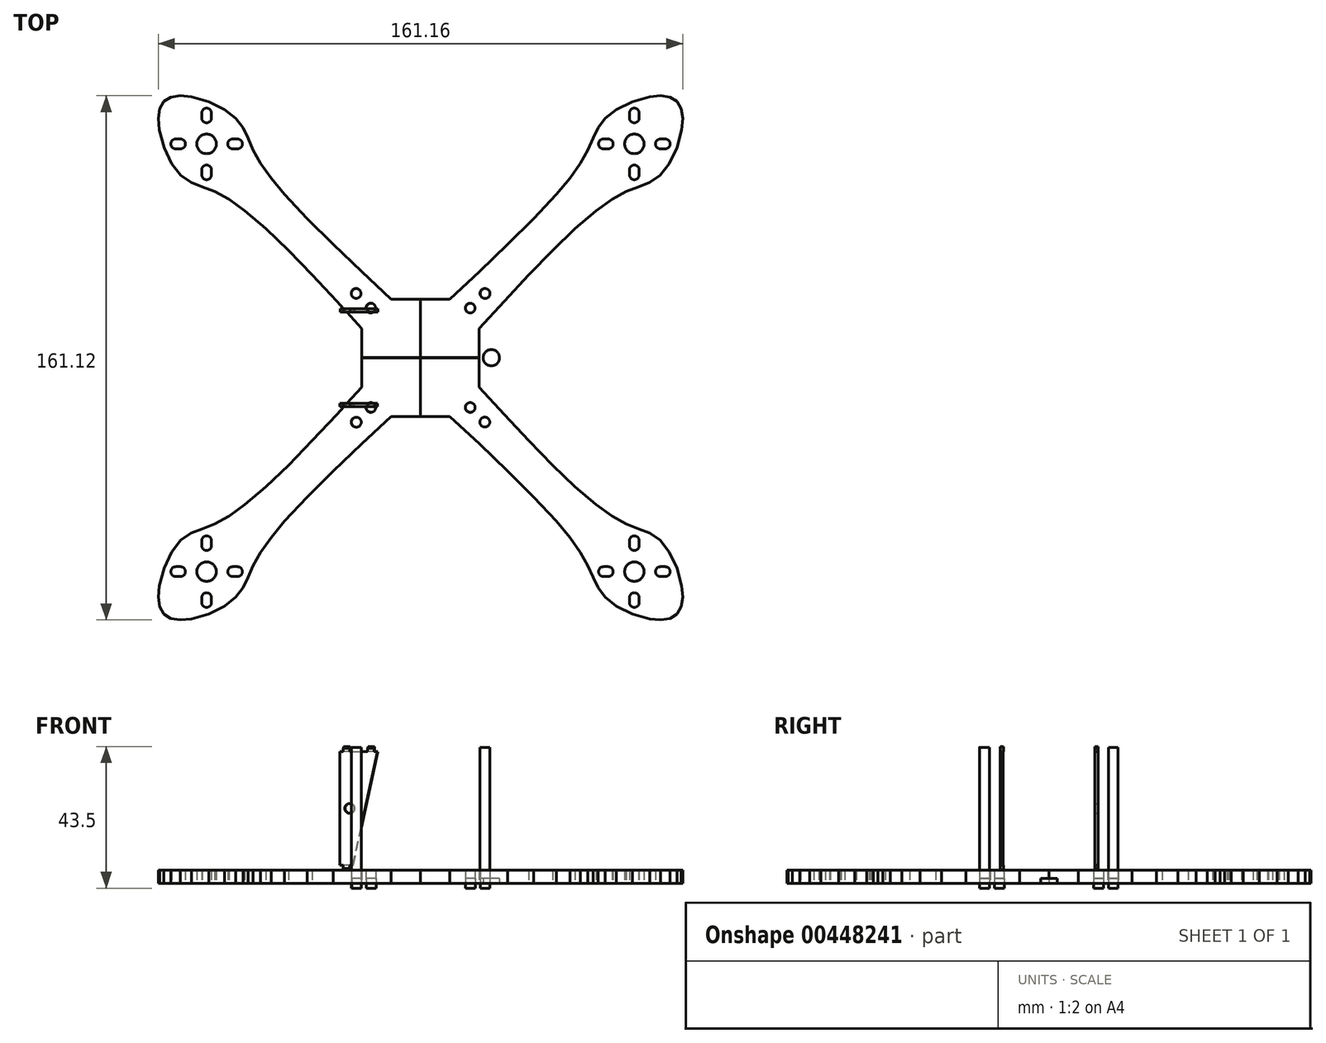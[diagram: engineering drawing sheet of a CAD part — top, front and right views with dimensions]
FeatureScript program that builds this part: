
annotation { "Feature Type Name" : "Feature", "Feature Type Description" : "" }
export const myFeature = defineFeature(function(context is Context, id is Id, definition is map)
    precondition{}
    {
        {
            var Q0;
            Q0=qCreatedBy(makeId("Top.planeOp"),FACE);
            var sketch = newSketch(context, id + "F0", { "sketchPlane" : qUnion([Q0])});
            skLineSegment(sketch, "E0", {"start": v(22.28, -31.26) * mm, "end": v(14.59, -22.9) * mm});
            skLineSegment(sketch, "E1", {"start": v(14.59, -22.9) * mm, "end": v(7.02, -14.81) * mm});
            skLineSegment(sketch, "E2", {"start": v(7.02, -14.81) * mm, "end": v(-0.3, -7.3) * mm});
            skLineSegment(sketch, "E3", {"start": v(-0.3, -7.3) * mm, "end": v(-7.23, -0.64) * mm});
            skLineSegment(sketch, "E4", {"start": v(-7.23, -0.64) * mm, "end": v(-13.66, 4.88) * mm});
            skLineSegment(sketch, "E5", {"start": v(-13.66, 4.88) * mm, "end": v(-18.55, 8.4) * mm});
            skLineSegment(sketch, "E6", {"start": v(-18.55, 8.4) * mm, "end": v(-22.93, 10.78) * mm});
            skLineSegment(sketch, "E7", {"start": v(-22.93, 10.78) * mm, "end": v(-26.8, 12.26) * mm});
            skLineSegment(sketch, "E8", {"start": v(-26.8, 12.26) * mm, "end": v(-30.23, 13.65) * mm});
            skLineSegment(sketch, "E9", {"start": v(-30.23, 13.65) * mm, "end": v(-33.32, 15.76) * mm});
            skLineSegment(sketch, "E10", {"start": v(-33.32, 15.76) * mm, "end": v(-36.16, 19.37) * mm});
            skLineSegment(sketch, "E11", {"start": v(-36.16, 19.37) * mm, "end": v(-38.52, 24.35) * mm});
            skLineSegment(sketch, "E12", {"start": v(-38.52, 24.35) * mm, "end": v(-40, 29.8) * mm});
            skLineSegment(sketch, "E13", {"start": v(-40, 29.8) * mm, "end": v(-40.28, 33.26) * mm});
            skLineSegment(sketch, "E14", {"start": v(-40.28, 33.26) * mm, "end": v(-39.85, 36.25) * mm});
            skLineSegment(sketch, "E15", {"start": v(-39.85, 36.25) * mm, "end": v(-38.57, 38.5) * mm});
            skLineSegment(sketch, "E16", {"start": v(-38.57, 38.5) * mm, "end": v(-36.39, 39.82) * mm});
            skLineSegment(sketch, "E17", {"start": v(-36.39, 39.82) * mm, "end": v(-33.49, 40.26) * mm});
            skLineSegment(sketch, "E18", {"start": v(-33.49, 40.26) * mm, "end": v(-30.13, 39.97) * mm});
            skLineSegment(sketch, "E19", {"start": v(-30.13, 39.97) * mm, "end": v(-24.8, 38.45) * mm});
            skLineSegment(sketch, "E20", {"start": v(-24.8, 38.45) * mm, "end": v(-19.92, 36.05) * mm});
            skLineSegment(sketch, "E21", {"start": v(-19.92, 36.05) * mm, "end": v(-16.43, 33.33) * mm});
            skLineSegment(sketch, "E22", {"start": v(-16.43, 33.33) * mm, "end": v(-14.24, 30.4) * mm});
            skLineSegment(sketch, "E23", {"start": v(-14.24, 30.4) * mm, "end": v(-12.7, 27.18) * mm});
            skLineSegment(sketch, "E24", {"start": v(-12.7, 27.18) * mm, "end": v(-11.15, 23.57) * mm});
            skLineSegment(sketch, "E25", {"start": v(-11.15, 23.57) * mm, "end": v(-8.9, 19.5) * mm});
            skLineSegment(sketch, "E26", {"start": v(-8.9, 19.5) * mm, "end": v(-5.63, 14.93) * mm});
            skLineSegment(sketch, "E27", {"start": v(-5.63, 14.93) * mm, "end": v(-1.47, 9.94) * mm});
            skLineSegment(sketch, "E28", {"start": v(-1.47, 9.94) * mm, "end": v(5.47, 2.49) * mm});
            skLineSegment(sketch, "E29", {"start": v(5.47, 2.49) * mm, "end": v(13.47, -5.48) * mm});
            skLineSegment(sketch, "E30", {"start": v(13.47, -5.48) * mm, "end": v(22.2, -13.78) * mm});
            skLineSegment(sketch, "E31", {"start": v(22.2, -13.78) * mm, "end": v(31.28, -22.26) * mm});
            skArc(sketch, "E32", {"start": v(-23.92, 17.44) * mm, "mid": v(-25.42, 18.94) * mm, "end": v(-26.92, 17.44) * mm});
            skArc(sketch, "E33", {"start": v(-26.92, 15.94) * mm, "mid": v(-25.42, 14.44) * mm, "end": v(-23.92, 15.94) * mm});
            skArc(sketch, "E34", {"start": v(-34.92, 26.94) * mm, "mid": v(-36.42, 25.44) * mm, "end": v(-34.92, 23.94) * mm});
            skArc(sketch, "E35", {"start": v(-33.42, 23.94) * mm, "mid": v(-31.92, 25.44) * mm, "end": v(-33.42, 26.94) * mm});
            skArc(sketch, "E36", {"start": v(-26.92, 33.44) * mm, "mid": v(-25.42, 31.94) * mm, "end": v(-23.92, 33.44) * mm});
            skArc(sketch, "E37", {"start": v(-23.92, 34.94) * mm, "mid": v(-25.42, 36.44) * mm, "end": v(-26.92, 34.94) * mm});
            skLineSegment(sketch, "E38", {"start": v(-26.92, 17.44) * mm, "end": v(-26.92, 15.94) * mm});
            skLineSegment(sketch, "E39", {"start": v(-23.92, 17.44) * mm, "end": v(-23.92, 15.94) * mm});
            skLineSegment(sketch, "E40", {"start": v(-34.92, 26.94) * mm, "end": v(-33.42, 26.94) * mm});
            skLineSegment(sketch, "E41", {"start": v(-34.92, 23.94) * mm, "end": v(-33.42, 23.94) * mm});
            skLineSegment(sketch, "E42", {"start": v(-26.92, 33.44) * mm, "end": v(-26.92, 34.94) * mm});
            skLineSegment(sketch, "E43", {"start": v(-23.92, 33.44) * mm, "end": v(-23.92, 34.94) * mm});
            skArc(sketch, "E44", {"start": v(-15.92, 23.94) * mm, "mid": v(-14.42, 25.44) * mm, "end": v(-15.92, 26.94) * mm});
            skArc(sketch, "E45", {"start": v(-17.42, 26.94) * mm, "mid": v(-18.92, 25.44) * mm, "end": v(-17.42, 23.94) * mm});
            skLineSegment(sketch, "E46", {"start": v(-17.42, 23.94) * mm, "end": v(-15.92, 23.94) * mm});
            skLineSegment(sketch, "E47", {"start": v(-17.42, 26.94) * mm, "end": v(-15.92, 26.94) * mm});
            skCircle(sketch, "E48", {"center": v(-25.43, 25.44) * mm, "radius": 3 * mm});
            skLineSegment(sketch, "E49", {"start": v(22.28, -40.26) * mm, "end": v(40.28, -40.26) * mm});
            skCircle(sketch, "E50", {"center": v(25.03, -25.01) * mm, "radius": 1.5 * mm});
            skLineSegment(sketch, "E51", {"start": v(22.28, -40.26) * mm, "end": v(22.28, -31.26) * mm});
            skLineSegment(sketch, "E52", {"start": v(40.28, -22.26) * mm, "end": v(31.28, -22.26) * mm});
            skCircle(sketch, "E53", {"center": v(20.51, -20.5) * mm, "radius": 1.5 * mm});
            skLineSegment(sketch, "E54", {"start": v(40.28, -22.26) * mm, "end": v(40.28, -40.26) * mm});
            skSolve(sketch);
        }
        {
            var Q0;
            Q0 = qSketchRegion(id + "F0", true);
            extrude(context, id + "F1", {"entities" : qUnion([Q0]), "depth" : 4 * mm});
        }
        {
            var Q0;
            Q0=makeQuery(id+"F1.opExtrude","SWEPT_BODY",BODY,{"disambiguationData":[OSD([sQuery(id+"F0.wireOp",EDGE,"E0"),sQuery(id+"F0.wireOp",EDGE,"E1"),sQuery(id+"F0.wireOp",EDGE,"E2"),sQuery(id+"F0.wireOp",EDGE,"E3"),sQuery(id+"F0.wireOp",EDGE,"E4"),sQuery(id+"F0.wireOp",EDGE,"E5"),sQuery(id+"F0.wireOp",EDGE,"E6"),sQuery(id+"F0.wireOp",EDGE,"E7"),sQuery(id+"F0.wireOp",EDGE,"E8"),sQuery(id+"F0.wireOp",EDGE,"E9"),sQuery(id+"F0.wireOp",EDGE,"E10"),sQuery(id+"F0.wireOp",EDGE,"E11"),sQuery(id+"F0.wireOp",EDGE,"E12"),sQuery(id+"F0.wireOp",EDGE,"E13"),sQuery(id+"F0.wireOp",EDGE,"E14"),sQuery(id+"F0.wireOp",EDGE,"E15"),sQuery(id+"F0.wireOp",EDGE,"E16"),sQuery(id+"F0.wireOp",EDGE,"E17"),sQuery(id+"F0.wireOp",EDGE,"E18"),sQuery(id+"F0.wireOp",EDGE,"E19"),sQuery(id+"F0.wireOp",EDGE,"E20"),sQuery(id+"F0.wireOp",EDGE,"E21"),sQuery(id+"F0.wireOp",EDGE,"E22"),sQuery(id+"F0.wireOp",EDGE,"E23"),sQuery(id+"F0.wireOp",EDGE,"E24"),sQuery(id+"F0.wireOp",EDGE,"E25"),sQuery(id+"F0.wireOp",EDGE,"E26"),sQuery(id+"F0.wireOp",EDGE,"E27"),sQuery(id+"F0.wireOp",EDGE,"E28"),sQuery(id+"F0.wireOp",EDGE,"E29"),sQuery(id+"F0.wireOp",EDGE,"E30"),sQuery(id+"F0.wireOp",EDGE,"E31"),sQuery(id+"F0.wireOp",EDGE,"E32"),sQuery(id+"F0.wireOp",EDGE,"E33"),sQuery(id+"F0.wireOp",EDGE,"E34"),sQuery(id+"F0.wireOp",EDGE,"E35"),sQuery(id+"F0.wireOp",EDGE,"E36"),sQuery(id+"F0.wireOp",EDGE,"E37"),sQuery(id+"F0.wireOp",EDGE,"E38"),sQuery(id+"F0.wireOp",EDGE,"E39"),sQuery(id+"F0.wireOp",EDGE,"E40"),sQuery(id+"F0.wireOp",EDGE,"E41"),sQuery(id+"F0.wireOp",EDGE,"E42"),sQuery(id+"F0.wireOp",EDGE,"E43"),sQuery(id+"F0.wireOp",EDGE,"E44"),sQuery(id+"F0.wireOp",EDGE,"E45"),sQuery(id+"F0.wireOp",EDGE,"E46"),sQuery(id+"F0.wireOp",EDGE,"E47"),sQuery(id+"F0.wireOp",EDGE,"E48"),sQuery(id+"F0.wireOp",EDGE,"E49"),sQuery(id+"F0.wireOp",EDGE,"E50"),sQuery(id+"F0.wireOp",EDGE,"E51"),sQuery(id+"F0.wireOp",EDGE,"E52"),sQuery(id+"F0.wireOp",EDGE,"E53"),sQuery(id+"F0.wireOp",EDGE,"E54")])]});
            transform(context, id + "F2", {"entities" : qUnion([Q0]), "transformType" : TransformType.TRANSLATION_3D, "dx" : -40.3 * mm, "dy" : 40.3 * mm, "dz" : 0 * mm, "makeCopy" : false});
        }
        {
            var Q0;
            Q0 = qSketchRegion(id + "F0", true);
            extrude(context, id + "F3", {"entities" : qUnion([Q0]), "depth" : 4 * mm});
        }
        {
            var Q0;
            Q0=makeQuery(id+"F3.opExtrude","SWEPT_BODY",BODY,{"disambiguationData":[OSD([sQuery(id+"F0.wireOp",EDGE,"E0"),sQuery(id+"F0.wireOp",EDGE,"E1"),sQuery(id+"F0.wireOp",EDGE,"E2"),sQuery(id+"F0.wireOp",EDGE,"E3"),sQuery(id+"F0.wireOp",EDGE,"E4"),sQuery(id+"F0.wireOp",EDGE,"E5"),sQuery(id+"F0.wireOp",EDGE,"E6"),sQuery(id+"F0.wireOp",EDGE,"E7"),sQuery(id+"F0.wireOp",EDGE,"E8"),sQuery(id+"F0.wireOp",EDGE,"E9"),sQuery(id+"F0.wireOp",EDGE,"E10"),sQuery(id+"F0.wireOp",EDGE,"E11"),sQuery(id+"F0.wireOp",EDGE,"E12"),sQuery(id+"F0.wireOp",EDGE,"E13"),sQuery(id+"F0.wireOp",EDGE,"E14"),sQuery(id+"F0.wireOp",EDGE,"E15"),sQuery(id+"F0.wireOp",EDGE,"E16"),sQuery(id+"F0.wireOp",EDGE,"E17"),sQuery(id+"F0.wireOp",EDGE,"E18"),sQuery(id+"F0.wireOp",EDGE,"E19"),sQuery(id+"F0.wireOp",EDGE,"E20"),sQuery(id+"F0.wireOp",EDGE,"E21"),sQuery(id+"F0.wireOp",EDGE,"E22"),sQuery(id+"F0.wireOp",EDGE,"E23"),sQuery(id+"F0.wireOp",EDGE,"E24"),sQuery(id+"F0.wireOp",EDGE,"E25"),sQuery(id+"F0.wireOp",EDGE,"E26"),sQuery(id+"F0.wireOp",EDGE,"E27"),sQuery(id+"F0.wireOp",EDGE,"E28"),sQuery(id+"F0.wireOp",EDGE,"E29"),sQuery(id+"F0.wireOp",EDGE,"E30"),sQuery(id+"F0.wireOp",EDGE,"E31"),sQuery(id+"F0.wireOp",EDGE,"E32"),sQuery(id+"F0.wireOp",EDGE,"E33"),sQuery(id+"F0.wireOp",EDGE,"E34"),sQuery(id+"F0.wireOp",EDGE,"E35"),sQuery(id+"F0.wireOp",EDGE,"E36"),sQuery(id+"F0.wireOp",EDGE,"E37"),sQuery(id+"F0.wireOp",EDGE,"E38"),sQuery(id+"F0.wireOp",EDGE,"E39"),sQuery(id+"F0.wireOp",EDGE,"E40"),sQuery(id+"F0.wireOp",EDGE,"E41"),sQuery(id+"F0.wireOp",EDGE,"E42"),sQuery(id+"F0.wireOp",EDGE,"E43"),sQuery(id+"F0.wireOp",EDGE,"E44"),sQuery(id+"F0.wireOp",EDGE,"E45"),sQuery(id+"F0.wireOp",EDGE,"E46"),sQuery(id+"F0.wireOp",EDGE,"E47"),sQuery(id+"F0.wireOp",EDGE,"E48"),sQuery(id+"F0.wireOp",EDGE,"E49"),sQuery(id+"F0.wireOp",EDGE,"E50"),sQuery(id+"F0.wireOp",EDGE,"E51"),sQuery(id+"F0.wireOp",EDGE,"E52"),sQuery(id+"F0.wireOp",EDGE,"E53"),sQuery(id+"F0.wireOp",EDGE,"E54")])]});
            var Q1;
            Q1=qCreatedBy(makeId("Front.planeOp"),FACE);
            mirror(context, id + "F4", {"entities" : qUnion([Q0]), "mirrorPlane" : qUnion([Q1])});
        }
        {
            var Q0;
            Q0=makeQuery(id+"F4.opPattern","COPY",BODY,{"derivedFrom":makeQuery(id+"F3.opExtrude","SWEPT_BODY",BODY,{"disambiguationData":[OSD([sQuery(id+"F0.wireOp",EDGE,"E0"),sQuery(id+"F0.wireOp",EDGE,"E1"),sQuery(id+"F0.wireOp",EDGE,"E2"),sQuery(id+"F0.wireOp",EDGE,"E3"),sQuery(id+"F0.wireOp",EDGE,"E4"),sQuery(id+"F0.wireOp",EDGE,"E5"),sQuery(id+"F0.wireOp",EDGE,"E6"),sQuery(id+"F0.wireOp",EDGE,"E7"),sQuery(id+"F0.wireOp",EDGE,"E8"),sQuery(id+"F0.wireOp",EDGE,"E9"),sQuery(id+"F0.wireOp",EDGE,"E10"),sQuery(id+"F0.wireOp",EDGE,"E11"),sQuery(id+"F0.wireOp",EDGE,"E12"),sQuery(id+"F0.wireOp",EDGE,"E13"),sQuery(id+"F0.wireOp",EDGE,"E14"),sQuery(id+"F0.wireOp",EDGE,"E15"),sQuery(id+"F0.wireOp",EDGE,"E16"),sQuery(id+"F0.wireOp",EDGE,"E17"),sQuery(id+"F0.wireOp",EDGE,"E18"),sQuery(id+"F0.wireOp",EDGE,"E19"),sQuery(id+"F0.wireOp",EDGE,"E20"),sQuery(id+"F0.wireOp",EDGE,"E21"),sQuery(id+"F0.wireOp",EDGE,"E22"),sQuery(id+"F0.wireOp",EDGE,"E23"),sQuery(id+"F0.wireOp",EDGE,"E24"),sQuery(id+"F0.wireOp",EDGE,"E25"),sQuery(id+"F0.wireOp",EDGE,"E26"),sQuery(id+"F0.wireOp",EDGE,"E27"),sQuery(id+"F0.wireOp",EDGE,"E28"),sQuery(id+"F0.wireOp",EDGE,"E29"),sQuery(id+"F0.wireOp",EDGE,"E30"),sQuery(id+"F0.wireOp",EDGE,"E31"),sQuery(id+"F0.wireOp",EDGE,"E32"),sQuery(id+"F0.wireOp",EDGE,"E33"),sQuery(id+"F0.wireOp",EDGE,"E34"),sQuery(id+"F0.wireOp",EDGE,"E35"),sQuery(id+"F0.wireOp",EDGE,"E36"),sQuery(id+"F0.wireOp",EDGE,"E37"),sQuery(id+"F0.wireOp",EDGE,"E38"),sQuery(id+"F0.wireOp",EDGE,"E39"),sQuery(id+"F0.wireOp",EDGE,"E40"),sQuery(id+"F0.wireOp",EDGE,"E41"),sQuery(id+"F0.wireOp",EDGE,"E42"),sQuery(id+"F0.wireOp",EDGE,"E43"),sQuery(id+"F0.wireOp",EDGE,"E44"),sQuery(id+"F0.wireOp",EDGE,"E45"),sQuery(id+"F0.wireOp",EDGE,"E46"),sQuery(id+"F0.wireOp",EDGE,"E47"),sQuery(id+"F0.wireOp",EDGE,"E48"),sQuery(id+"F0.wireOp",EDGE,"E49"),sQuery(id+"F0.wireOp",EDGE,"E50"),sQuery(id+"F0.wireOp",EDGE,"E51"),sQuery(id+"F0.wireOp",EDGE,"E52"),sQuery(id+"F0.wireOp",EDGE,"E53"),sQuery(id+"F0.wireOp",EDGE,"E54")])]}),"instanceName":"1"});
            transform(context, id + "F5", {"entities" : qUnion([Q0]), "transformType" : TransformType.TRANSLATION_3D, "dx" : -40.3 * mm, "dy" : -40.3 * mm, "dz" : 0 * mm, "makeCopy" : false});
        }
        {
            var Q0;
            Q0=makeQuery(id+"F3.opExtrude","SWEPT_BODY",BODY,{"disambiguationData":[OSD([sQuery(id+"F0.wireOp",EDGE,"E0"),sQuery(id+"F0.wireOp",EDGE,"E1"),sQuery(id+"F0.wireOp",EDGE,"E2"),sQuery(id+"F0.wireOp",EDGE,"E3"),sQuery(id+"F0.wireOp",EDGE,"E4"),sQuery(id+"F0.wireOp",EDGE,"E5"),sQuery(id+"F0.wireOp",EDGE,"E6"),sQuery(id+"F0.wireOp",EDGE,"E7"),sQuery(id+"F0.wireOp",EDGE,"E8"),sQuery(id+"F0.wireOp",EDGE,"E9"),sQuery(id+"F0.wireOp",EDGE,"E10"),sQuery(id+"F0.wireOp",EDGE,"E11"),sQuery(id+"F0.wireOp",EDGE,"E12"),sQuery(id+"F0.wireOp",EDGE,"E13"),sQuery(id+"F0.wireOp",EDGE,"E14"),sQuery(id+"F0.wireOp",EDGE,"E15"),sQuery(id+"F0.wireOp",EDGE,"E16"),sQuery(id+"F0.wireOp",EDGE,"E17"),sQuery(id+"F0.wireOp",EDGE,"E18"),sQuery(id+"F0.wireOp",EDGE,"E19"),sQuery(id+"F0.wireOp",EDGE,"E20"),sQuery(id+"F0.wireOp",EDGE,"E21"),sQuery(id+"F0.wireOp",EDGE,"E22"),sQuery(id+"F0.wireOp",EDGE,"E23"),sQuery(id+"F0.wireOp",EDGE,"E24"),sQuery(id+"F0.wireOp",EDGE,"E25"),sQuery(id+"F0.wireOp",EDGE,"E26"),sQuery(id+"F0.wireOp",EDGE,"E27"),sQuery(id+"F0.wireOp",EDGE,"E28"),sQuery(id+"F0.wireOp",EDGE,"E29"),sQuery(id+"F0.wireOp",EDGE,"E30"),sQuery(id+"F0.wireOp",EDGE,"E31"),sQuery(id+"F0.wireOp",EDGE,"E32"),sQuery(id+"F0.wireOp",EDGE,"E33"),sQuery(id+"F0.wireOp",EDGE,"E34"),sQuery(id+"F0.wireOp",EDGE,"E35"),sQuery(id+"F0.wireOp",EDGE,"E36"),sQuery(id+"F0.wireOp",EDGE,"E37"),sQuery(id+"F0.wireOp",EDGE,"E38"),sQuery(id+"F0.wireOp",EDGE,"E39"),sQuery(id+"F0.wireOp",EDGE,"E40"),sQuery(id+"F0.wireOp",EDGE,"E41"),sQuery(id+"F0.wireOp",EDGE,"E42"),sQuery(id+"F0.wireOp",EDGE,"E43"),sQuery(id+"F0.wireOp",EDGE,"E44"),sQuery(id+"F0.wireOp",EDGE,"E45"),sQuery(id+"F0.wireOp",EDGE,"E46"),sQuery(id+"F0.wireOp",EDGE,"E47"),sQuery(id+"F0.wireOp",EDGE,"E48"),sQuery(id+"F0.wireOp",EDGE,"E49"),sQuery(id+"F0.wireOp",EDGE,"E50"),sQuery(id+"F0.wireOp",EDGE,"E51"),sQuery(id+"F0.wireOp",EDGE,"E52"),sQuery(id+"F0.wireOp",EDGE,"E53"),sQuery(id+"F0.wireOp",EDGE,"E54")])]});
            deleteBodies(context, id + "F6", {"entities" : qUnion([Q0])});
        }
        {
            var Q0;
            Q0=makeQuery(id+"F1.opExtrude","SWEPT_BODY",BODY,{"disambiguationData":[OSD([sQuery(id+"F0.wireOp",EDGE,"E0"),sQuery(id+"F0.wireOp",EDGE,"E1"),sQuery(id+"F0.wireOp",EDGE,"E2"),sQuery(id+"F0.wireOp",EDGE,"E3"),sQuery(id+"F0.wireOp",EDGE,"E4"),sQuery(id+"F0.wireOp",EDGE,"E5"),sQuery(id+"F0.wireOp",EDGE,"E6"),sQuery(id+"F0.wireOp",EDGE,"E7"),sQuery(id+"F0.wireOp",EDGE,"E8"),sQuery(id+"F0.wireOp",EDGE,"E9"),sQuery(id+"F0.wireOp",EDGE,"E10"),sQuery(id+"F0.wireOp",EDGE,"E11"),sQuery(id+"F0.wireOp",EDGE,"E12"),sQuery(id+"F0.wireOp",EDGE,"E13"),sQuery(id+"F0.wireOp",EDGE,"E14"),sQuery(id+"F0.wireOp",EDGE,"E15"),sQuery(id+"F0.wireOp",EDGE,"E16"),sQuery(id+"F0.wireOp",EDGE,"E17"),sQuery(id+"F0.wireOp",EDGE,"E18"),sQuery(id+"F0.wireOp",EDGE,"E19"),sQuery(id+"F0.wireOp",EDGE,"E20"),sQuery(id+"F0.wireOp",EDGE,"E21"),sQuery(id+"F0.wireOp",EDGE,"E22"),sQuery(id+"F0.wireOp",EDGE,"E23"),sQuery(id+"F0.wireOp",EDGE,"E24"),sQuery(id+"F0.wireOp",EDGE,"E25"),sQuery(id+"F0.wireOp",EDGE,"E26"),sQuery(id+"F0.wireOp",EDGE,"E27"),sQuery(id+"F0.wireOp",EDGE,"E28"),sQuery(id+"F0.wireOp",EDGE,"E29"),sQuery(id+"F0.wireOp",EDGE,"E30"),sQuery(id+"F0.wireOp",EDGE,"E31"),sQuery(id+"F0.wireOp",EDGE,"E32"),sQuery(id+"F0.wireOp",EDGE,"E33"),sQuery(id+"F0.wireOp",EDGE,"E34"),sQuery(id+"F0.wireOp",EDGE,"E35"),sQuery(id+"F0.wireOp",EDGE,"E36"),sQuery(id+"F0.wireOp",EDGE,"E37"),sQuery(id+"F0.wireOp",EDGE,"E38"),sQuery(id+"F0.wireOp",EDGE,"E39"),sQuery(id+"F0.wireOp",EDGE,"E40"),sQuery(id+"F0.wireOp",EDGE,"E41"),sQuery(id+"F0.wireOp",EDGE,"E42"),sQuery(id+"F0.wireOp",EDGE,"E43"),sQuery(id+"F0.wireOp",EDGE,"E44"),sQuery(id+"F0.wireOp",EDGE,"E45"),sQuery(id+"F0.wireOp",EDGE,"E46"),sQuery(id+"F0.wireOp",EDGE,"E47"),sQuery(id+"F0.wireOp",EDGE,"E48"),sQuery(id+"F0.wireOp",EDGE,"E49"),sQuery(id+"F0.wireOp",EDGE,"E50"),sQuery(id+"F0.wireOp",EDGE,"E51"),sQuery(id+"F0.wireOp",EDGE,"E52"),sQuery(id+"F0.wireOp",EDGE,"E53"),sQuery(id+"F0.wireOp",EDGE,"E54")])]});
            var Q1;
            Q1=qCreatedBy(makeId("Right.planeOp"),FACE);
            mirror(context, id + "F7", {"entities" : qUnion([Q0]), "mirrorPlane" : qUnion([Q1])});
        }
        {
            var Q0;
            Q0=makeQuery(id+"F7.opPattern","COPY",BODY,{"derivedFrom":makeQuery(id+"F1.opExtrude","SWEPT_BODY",BODY,{"disambiguationData":[OSD([sQuery(id+"F0.wireOp",EDGE,"E0"),sQuery(id+"F0.wireOp",EDGE,"E1"),sQuery(id+"F0.wireOp",EDGE,"E2"),sQuery(id+"F0.wireOp",EDGE,"E3"),sQuery(id+"F0.wireOp",EDGE,"E4"),sQuery(id+"F0.wireOp",EDGE,"E5"),sQuery(id+"F0.wireOp",EDGE,"E6"),sQuery(id+"F0.wireOp",EDGE,"E7"),sQuery(id+"F0.wireOp",EDGE,"E8"),sQuery(id+"F0.wireOp",EDGE,"E9"),sQuery(id+"F0.wireOp",EDGE,"E10"),sQuery(id+"F0.wireOp",EDGE,"E11"),sQuery(id+"F0.wireOp",EDGE,"E12"),sQuery(id+"F0.wireOp",EDGE,"E13"),sQuery(id+"F0.wireOp",EDGE,"E14"),sQuery(id+"F0.wireOp",EDGE,"E15"),sQuery(id+"F0.wireOp",EDGE,"E16"),sQuery(id+"F0.wireOp",EDGE,"E17"),sQuery(id+"F0.wireOp",EDGE,"E18"),sQuery(id+"F0.wireOp",EDGE,"E19"),sQuery(id+"F0.wireOp",EDGE,"E20"),sQuery(id+"F0.wireOp",EDGE,"E21"),sQuery(id+"F0.wireOp",EDGE,"E22"),sQuery(id+"F0.wireOp",EDGE,"E23"),sQuery(id+"F0.wireOp",EDGE,"E24"),sQuery(id+"F0.wireOp",EDGE,"E25"),sQuery(id+"F0.wireOp",EDGE,"E26"),sQuery(id+"F0.wireOp",EDGE,"E27"),sQuery(id+"F0.wireOp",EDGE,"E28"),sQuery(id+"F0.wireOp",EDGE,"E29"),sQuery(id+"F0.wireOp",EDGE,"E30"),sQuery(id+"F0.wireOp",EDGE,"E31"),sQuery(id+"F0.wireOp",EDGE,"E32"),sQuery(id+"F0.wireOp",EDGE,"E33"),sQuery(id+"F0.wireOp",EDGE,"E34"),sQuery(id+"F0.wireOp",EDGE,"E35"),sQuery(id+"F0.wireOp",EDGE,"E36"),sQuery(id+"F0.wireOp",EDGE,"E37"),sQuery(id+"F0.wireOp",EDGE,"E38"),sQuery(id+"F0.wireOp",EDGE,"E39"),sQuery(id+"F0.wireOp",EDGE,"E40"),sQuery(id+"F0.wireOp",EDGE,"E41"),sQuery(id+"F0.wireOp",EDGE,"E42"),sQuery(id+"F0.wireOp",EDGE,"E43"),sQuery(id+"F0.wireOp",EDGE,"E44"),sQuery(id+"F0.wireOp",EDGE,"E45"),sQuery(id+"F0.wireOp",EDGE,"E46"),sQuery(id+"F0.wireOp",EDGE,"E47"),sQuery(id+"F0.wireOp",EDGE,"E48"),sQuery(id+"F0.wireOp",EDGE,"E49"),sQuery(id+"F0.wireOp",EDGE,"E50"),sQuery(id+"F0.wireOp",EDGE,"E51"),sQuery(id+"F0.wireOp",EDGE,"E52"),sQuery(id+"F0.wireOp",EDGE,"E53"),sQuery(id+"F0.wireOp",EDGE,"E54")])]}),"instanceName":"1"});
            var Q1;
            Q1=qCreatedBy(makeId("Front.planeOp"),FACE);
            mirror(context, id + "F8", {"entities" : qUnion([Q0]), "mirrorPlane" : qUnion([Q1])});
        }
        {
            var Q0;
            Q0=qCreatedBy(makeId("Top.planeOp"),FACE);
            var sketch = newSketch(context, id + "F9", { "sketchPlane" : qUnion([Q0])});
            skLineSegment(sketch, "E55", {"start": v(-21.78, -21.9) * mm, "end": v(-25.39, -18.3) * mm});
            skLineSegment(sketch, "E56", {"start": v(-21.78, 21.9) * mm, "end": v(-25.3, 18.38) * mm});
            skLineSegment(sketch, "E57", {"start": v(-25.88, 16.76) * mm, "end": v(-24.97, 12.73) * mm});
            skLineSegment(sketch, "E58", {"start": v(-24.97, 12.73) * mm, "end": v(-23.5, 8.88) * mm});
            skLineSegment(sketch, "E59", {"start": v(-23.5, 8.88) * mm, "end": v(-22, 5.17) * mm});
            skLineSegment(sketch, "E60", {"start": v(-22, 5.17) * mm, "end": v(-21.02, 1.6) * mm});
            skLineSegment(sketch, "E61", {"start": v(-21.02, 1.6) * mm, "end": v(-21.1, -1.9) * mm});
            skLineSegment(sketch, "E62", {"start": v(-21.1, -1.9) * mm, "end": v(-22.18, -5.3) * mm});
            skLineSegment(sketch, "E63", {"start": v(-22.18, -5.3) * mm, "end": v(-23.7, -8.82) * mm});
            skLineSegment(sketch, "E64", {"start": v(-23.7, -8.82) * mm, "end": v(-25.15, -12.6) * mm});
            skLineSegment(sketch, "E65", {"start": v(-25.15, -12.6) * mm, "end": v(-25.97, -16.73) * mm});
            skLineSegment(sketch, "E66", {"start": v(21.98, -21.89) * mm, "end": v(20.2, -22.93) * mm});
            skLineSegment(sketch, "E67", {"start": v(20.2, -22.93) * mm, "end": v(18.03, -23.06) * mm});
            skLineSegment(sketch, "E68", {"start": v(18.03, -23.06) * mm, "end": v(15.54, -22.51) * mm});
            skLineSegment(sketch, "E69", {"start": v(15.54, -22.51) * mm, "end": v(12.78, -21.53) * mm});
            skLineSegment(sketch, "E70", {"start": v(12.78, -21.53) * mm, "end": v(8.77, -19.95) * mm});
            skLineSegment(sketch, "E71", {"start": v(8.77, -19.95) * mm, "end": v(4.5, -18.58) * mm});
            skLineSegment(sketch, "E72", {"start": v(4.5, -18.58) * mm, "end": v(0.1, -18) * mm});
            skLineSegment(sketch, "E73", {"start": v(0.1, -18) * mm, "end": v(-4.31, -18.57) * mm});
            skLineSegment(sketch, "E74", {"start": v(-4.31, -18.57) * mm, "end": v(-8.59, -19.93) * mm});
            skLineSegment(sketch, "E75", {"start": v(-8.59, -19.93) * mm, "end": v(-12.6, -21.5) * mm});
            skLineSegment(sketch, "E76", {"start": v(-12.6, -21.5) * mm, "end": v(-15.37, -22.48) * mm});
            skLineSegment(sketch, "E77", {"start": v(-15.37, -22.48) * mm, "end": v(-17.86, -23.04) * mm});
            skLineSegment(sketch, "E78", {"start": v(-17.86, -23.04) * mm, "end": v(-20, -22.92) * mm});
            skLineSegment(sketch, "E79", {"start": v(-20, -22.92) * mm, "end": v(-21.76, -21.92) * mm});
            skLineSegment(sketch, "E80", {"start": v(-21.76, 21.92) * mm, "end": v(-19.99, 22.94) * mm});
            skLineSegment(sketch, "E81", {"start": v(-19.99, 22.94) * mm, "end": v(-17.84, 23.06) * mm});
            skLineSegment(sketch, "E82", {"start": v(-17.84, 23.06) * mm, "end": v(-15.35, 22.51) * mm});
            skLineSegment(sketch, "E83", {"start": v(-15.35, 22.51) * mm, "end": v(-12.6, 21.53) * mm});
            skLineSegment(sketch, "E84", {"start": v(-12.6, 21.53) * mm, "end": v(-8.58, 19.95) * mm});
            skLineSegment(sketch, "E85", {"start": v(-8.58, 19.95) * mm, "end": v(-4.31, 18.58) * mm});
            skLineSegment(sketch, "E86", {"start": v(-4.31, 18.58) * mm, "end": v(0.1, 18) * mm});
            skLineSegment(sketch, "E87", {"start": v(0.1, 18) * mm, "end": v(4.5, 18.57) * mm});
            skLineSegment(sketch, "E88", {"start": v(4.5, 18.57) * mm, "end": v(8.78, 19.92) * mm});
            skLineSegment(sketch, "E89", {"start": v(8.78, 19.92) * mm, "end": v(12.8, 21.5) * mm});
            skLineSegment(sketch, "E90", {"start": v(12.8, 21.5) * mm, "end": v(15.57, 22.47) * mm});
            skLineSegment(sketch, "E91", {"start": v(15.57, 22.47) * mm, "end": v(18.06, 23.03) * mm});
            skLineSegment(sketch, "E92", {"start": v(18.06, 23.03) * mm, "end": v(20.2, 22.9) * mm});
            skLineSegment(sketch, "E93", {"start": v(20.2, 22.9) * mm, "end": v(21.97, 21.89) * mm});
            skLineSegment(sketch, "E94", {"start": v(21.99, 21.88) * mm, "end": v(24.06, 18.68) * mm});
            skLineSegment(sketch, "E95", {"start": v(24.06, 18.68) * mm, "end": v(25.26, 14.51) * mm});
            skLineSegment(sketch, "E96", {"start": v(25.26, 14.51) * mm, "end": v(25.8, 9.64) * mm});
            skLineSegment(sketch, "E97", {"start": v(25.8, 9.64) * mm, "end": v(25.97, 3.34) * mm});
            skLineSegment(sketch, "E98", {"start": v(25.97, 3.34) * mm, "end": v(25.97, -3.19) * mm});
            skLineSegment(sketch, "E99", {"start": v(25.97, -3.19) * mm, "end": v(25.82, -9.52) * mm});
            skLineSegment(sketch, "E100", {"start": v(25.82, -9.52) * mm, "end": v(25.12, -15.22) * mm});
            skLineSegment(sketch, "E101", {"start": v(25.12, -15.22) * mm, "end": v(23.94, -18.98) * mm});
            skLineSegment(sketch, "E102", {"start": v(23.94, -18.98) * mm, "end": v(21.98, -21.89) * mm});
            skArc(sketch, "E103", {"start": v(21.99, 21.88) * mm, "mid": v(21.98, 21.88) * mm, "end": v(21.97, 21.89) * mm});
            skArc(sketch, "E104", {"start": v(-25.3, 18.38) * mm, "mid": v(-25.77, 17.64) * mm, "end": v(-25.88, 16.76) * mm});
            skArc(sketch, "E105", {"start": v(-21.76, 21.92) * mm, "mid": v(-21.77, 21.91) * mm, "end": v(-21.78, 21.9) * mm});
            skArc(sketch, "E106", {"start": v(-21.78, -21.9) * mm, "mid": v(-21.77, -21.91) * mm, "end": v(-21.76, -21.92) * mm});
            skLineSegment(sketch, "E107", {"start": v(-25.38, -18.3) * mm, "end": v(-21.8, -21.89) * mm});
            skLineSegment(sketch, "E108", {"start": v(-25.97, -16.73) * mm, "end": v(-25.97, -16.8) * mm});
            skArc(sketch, "E109", {"start": v(-25.97, -16.8) * mm, "mid": v(-25.83, -17.6) * mm, "end": v(-25.38, -18.3) * mm});
            skCircle(sketch, "E110", {"center": v(15.34, 15.25) * mm, "radius": 1.5 * mm});
            skCircle(sketch, "E111", {"center": v(15.34, -15.25) * mm, "radius": 1.5 * mm});
            skCircle(sketch, "E112", {"center": v(-15.16, -15.25) * mm, "radius": 1.5 * mm});
            skCircle(sketch, "E113", {"center": v(-15.16, 15.25) * mm, "radius": 1.5 * mm});
            skCircle(sketch, "E114", {"center": v(19.86, -19.77) * mm, "radius": 1.5 * mm});
            skCircle(sketch, "E115", {"center": v(19.86, 19.77) * mm, "radius": 1.5 * mm});
            skCircle(sketch, "E116", {"center": v(-19.67, 19.77) * mm, "radius": 1.5 * mm});
            skCircle(sketch, "E117", {"center": v(-19.63, -19.8) * mm, "radius": 1.5 * mm});
            skSolve(sketch);
        }
        {
            var Q0;
            Q0 = qSketchRegion(id + "F9", true);
            extrude(context, id + "F10", {"entities" : qUnion([Q0]), "depth" : 1.5 * mm});
        }
        {
            var Q0;
            Q0=makeQuery(id+"F10.opExtrude","SWEPT_BODY",BODY,{"disambiguationData":[OSD([sQuery(id+"F9.wireOp",EDGE,"E55"),sQuery(id+"F9.wireOp",EDGE,"E56"),sQuery(id+"F9.wireOp",EDGE,"E57"),sQuery(id+"F9.wireOp",EDGE,"E58"),sQuery(id+"F9.wireOp",EDGE,"E59"),sQuery(id+"F9.wireOp",EDGE,"E60"),sQuery(id+"F9.wireOp",EDGE,"E61"),sQuery(id+"F9.wireOp",EDGE,"E62"),sQuery(id+"F9.wireOp",EDGE,"E63"),sQuery(id+"F9.wireOp",EDGE,"E64"),sQuery(id+"F9.wireOp",EDGE,"E65"),sQuery(id+"F9.wireOp",EDGE,"E66"),sQuery(id+"F9.wireOp",EDGE,"E67"),sQuery(id+"F9.wireOp",EDGE,"E68"),sQuery(id+"F9.wireOp",EDGE,"E69"),sQuery(id+"F9.wireOp",EDGE,"E70"),sQuery(id+"F9.wireOp",EDGE,"E71"),sQuery(id+"F9.wireOp",EDGE,"E72"),sQuery(id+"F9.wireOp",EDGE,"E73"),sQuery(id+"F9.wireOp",EDGE,"E74"),sQuery(id+"F9.wireOp",EDGE,"E75"),sQuery(id+"F9.wireOp",EDGE,"E76"),sQuery(id+"F9.wireOp",EDGE,"E77"),sQuery(id+"F9.wireOp",EDGE,"E78"),sQuery(id+"F9.wireOp",EDGE,"E79"),sQuery(id+"F9.wireOp",EDGE,"E80"),sQuery(id+"F9.wireOp",EDGE,"E81"),sQuery(id+"F9.wireOp",EDGE,"E82"),sQuery(id+"F9.wireOp",EDGE,"E83"),sQuery(id+"F9.wireOp",EDGE,"E84"),sQuery(id+"F9.wireOp",EDGE,"E85"),sQuery(id+"F9.wireOp",EDGE,"E86"),sQuery(id+"F9.wireOp",EDGE,"E87"),sQuery(id+"F9.wireOp",EDGE,"E88"),sQuery(id+"F9.wireOp",EDGE,"E89"),sQuery(id+"F9.wireOp",EDGE,"E90"),sQuery(id+"F9.wireOp",EDGE,"E91"),sQuery(id+"F9.wireOp",EDGE,"E92"),sQuery(id+"F9.wireOp",EDGE,"E93"),sQuery(id+"F9.wireOp",EDGE,"E94"),sQuery(id+"F9.wireOp",EDGE,"E95"),sQuery(id+"F9.wireOp",EDGE,"E96"),sQuery(id+"F9.wireOp",EDGE,"E97"),sQuery(id+"F9.wireOp",EDGE,"E98"),sQuery(id+"F9.wireOp",EDGE,"E99"),sQuery(id+"F9.wireOp",EDGE,"E100"),sQuery(id+"F9.wireOp",EDGE,"E101"),sQuery(id+"F9.wireOp",EDGE,"E102"),sQuery(id+"F9.wireOp",EDGE,"E103"),sQuery(id+"F9.wireOp",EDGE,"E104"),sQuery(id+"F9.wireOp",EDGE,"E105"),sQuery(id+"F9.wireOp",EDGE,"E106"),sQuery(id+"F9.wireOp",EDGE,"E107"),sQuery(id+"F9.wireOp",EDGE,"E108"),sQuery(id+"F9.wireOp",EDGE,"E109"),sQuery(id+"F9.wireOp",EDGE,"E110"),sQuery(id+"F9.wireOp",EDGE,"E111"),sQuery(id+"F9.wireOp",EDGE,"E112"),sQuery(id+"F9.wireOp",EDGE,"E113"),sQuery(id+"F9.wireOp",EDGE,"E114"),sQuery(id+"F9.wireOp",EDGE,"E115"),sQuery(id+"F9.wireOp",EDGE,"E116"),sQuery(id+"F9.wireOp",EDGE,"E117")])]});
            transform(context, id + "F11", {"entities" : qUnion([Q0]), "transformType" : TransformType.TRANSLATION_3D, "dx" : 0 * mm, "dy" : 0 * mm, "dz" : -1.5 * mm, "makeCopy" : false});
        }
        {
            var Q0;
            Q0=qCreatedBy(makeId("Top.planeOp"),FACE);
            var sketch = newSketch(context, id + "F12", { "sketchPlane" : qUnion([Q0])});
            skLineSegment(sketch, "E118", {"start": v(-21.66, -14) * mm, "end": v(-23.66, -14) * mm});
            skLineSegment(sketch, "E119", {"start": v(-21.66, -15) * mm, "end": v(-23.66, -15) * mm});
            skLineSegment(sketch, "E120", {"start": v(-21.66, 15.1) * mm, "end": v(-23.66, 15.1) * mm});
            skLineSegment(sketch, "E121", {"start": v(-21.66, 14.1) * mm, "end": v(-23.66, 14.1) * mm});
            skLineSegment(sketch, "E122", {"start": v(-21.78, -21.9) * mm, "end": v(-25.39, -18.3) * mm});
            skLineSegment(sketch, "E123", {"start": v(-21.78, 21.9) * mm, "end": v(-25.3, 18.38) * mm});
            skLineSegment(sketch, "E124", {"start": v(-25.88, 16.76) * mm, "end": v(-24.97, 12.73) * mm});
            skLineSegment(sketch, "E125", {"start": v(-24.97, 12.73) * mm, "end": v(-23.5, 8.88) * mm});
            skLineSegment(sketch, "E126", {"start": v(-23.5, 8.88) * mm, "end": v(-22, 5.17) * mm});
            skLineSegment(sketch, "E127", {"start": v(-22, 5.17) * mm, "end": v(-21.02, 1.6) * mm});
            skLineSegment(sketch, "E128", {"start": v(-21.02, 1.6) * mm, "end": v(-21.1, -1.9) * mm});
            skLineSegment(sketch, "E129", {"start": v(-21.1, -1.9) * mm, "end": v(-22.18, -5.3) * mm});
            skLineSegment(sketch, "E130", {"start": v(-22.18, -5.3) * mm, "end": v(-23.7, -8.82) * mm});
            skLineSegment(sketch, "E131", {"start": v(-23.7, -8.82) * mm, "end": v(-25.15, -12.6) * mm});
            skLineSegment(sketch, "E132", {"start": v(-25.15, -12.6) * mm, "end": v(-25.97, -16.73) * mm});
            skLineSegment(sketch, "E133", {"start": v(21.98, -21.89) * mm, "end": v(20.2, -22.93) * mm});
            skLineSegment(sketch, "E134", {"start": v(20.2, -22.93) * mm, "end": v(18.03, -23.06) * mm});
            skLineSegment(sketch, "E135", {"start": v(18.03, -23.06) * mm, "end": v(15.54, -22.51) * mm});
            skLineSegment(sketch, "E136", {"start": v(15.54, -22.51) * mm, "end": v(12.78, -21.53) * mm});
            skLineSegment(sketch, "E137", {"start": v(12.78, -21.53) * mm, "end": v(8.77, -19.95) * mm});
            skLineSegment(sketch, "E138", {"start": v(8.77, -19.95) * mm, "end": v(4.5, -18.58) * mm});
            skLineSegment(sketch, "E139", {"start": v(4.5, -18.58) * mm, "end": v(0.1, -18) * mm});
            skLineSegment(sketch, "E140", {"start": v(0.1, -18) * mm, "end": v(-4.31, -18.57) * mm});
            skLineSegment(sketch, "E141", {"start": v(-4.31, -18.57) * mm, "end": v(-8.59, -19.93) * mm});
            skLineSegment(sketch, "E142", {"start": v(-8.59, -19.93) * mm, "end": v(-12.6, -21.5) * mm});
            skLineSegment(sketch, "E143", {"start": v(-12.6, -21.5) * mm, "end": v(-15.37, -22.48) * mm});
            skLineSegment(sketch, "E144", {"start": v(-15.37, -22.48) * mm, "end": v(-17.86, -23.04) * mm});
            skLineSegment(sketch, "E145", {"start": v(-17.86, -23.04) * mm, "end": v(-20, -22.92) * mm});
            skLineSegment(sketch, "E146", {"start": v(-20, -22.92) * mm, "end": v(-21.76, -21.92) * mm});
            skLineSegment(sketch, "E147", {"start": v(-21.76, 21.92) * mm, "end": v(-19.99, 22.94) * mm});
            skLineSegment(sketch, "E148", {"start": v(-19.99, 22.94) * mm, "end": v(-17.84, 23.06) * mm});
            skLineSegment(sketch, "E149", {"start": v(-17.84, 23.06) * mm, "end": v(-15.35, 22.51) * mm});
            skLineSegment(sketch, "E150", {"start": v(-15.35, 22.51) * mm, "end": v(-12.6, 21.53) * mm});
            skLineSegment(sketch, "E151", {"start": v(-12.6, 21.53) * mm, "end": v(-8.58, 19.95) * mm});
            skLineSegment(sketch, "E152", {"start": v(-8.58, 19.95) * mm, "end": v(-4.31, 18.58) * mm});
            skLineSegment(sketch, "E153", {"start": v(-4.31, 18.58) * mm, "end": v(0.1, 18) * mm});
            skLineSegment(sketch, "E154", {"start": v(0.1, 18) * mm, "end": v(4.5, 18.57) * mm});
            skLineSegment(sketch, "E155", {"start": v(4.5, 18.57) * mm, "end": v(8.78, 19.92) * mm});
            skLineSegment(sketch, "E156", {"start": v(8.78, 19.92) * mm, "end": v(12.8, 21.5) * mm});
            skLineSegment(sketch, "E157", {"start": v(12.8, 21.5) * mm, "end": v(15.57, 22.47) * mm});
            skLineSegment(sketch, "E158", {"start": v(15.57, 22.47) * mm, "end": v(18.06, 23.03) * mm});
            skLineSegment(sketch, "E159", {"start": v(18.06, 23.03) * mm, "end": v(20.2, 22.9) * mm});
            skLineSegment(sketch, "E160", {"start": v(20.2, 22.9) * mm, "end": v(21.97, 21.89) * mm});
            skLineSegment(sketch, "E161", {"start": v(21.99, 21.88) * mm, "end": v(24.06, 18.68) * mm});
            skLineSegment(sketch, "E162", {"start": v(24.06, 18.68) * mm, "end": v(25.26, 14.51) * mm});
            skLineSegment(sketch, "E163", {"start": v(25.26, 14.51) * mm, "end": v(25.8, 9.64) * mm});
            skLineSegment(sketch, "E164", {"start": v(25.8, 9.64) * mm, "end": v(25.97, 3.34) * mm});
            skLineSegment(sketch, "E165", {"start": v(25.97, 3.34) * mm, "end": v(25.97, -3.19) * mm});
            skLineSegment(sketch, "E166", {"start": v(25.97, -3.19) * mm, "end": v(25.82, -9.52) * mm});
            skLineSegment(sketch, "E167", {"start": v(25.82, -9.52) * mm, "end": v(25.12, -15.22) * mm});
            skLineSegment(sketch, "E168", {"start": v(25.12, -15.22) * mm, "end": v(23.94, -18.98) * mm});
            skLineSegment(sketch, "E169", {"start": v(23.94, -18.98) * mm, "end": v(21.98, -21.89) * mm});
            skArc(sketch, "E170", {"start": v(21.99, 21.88) * mm, "mid": v(21.98, 21.88) * mm, "end": v(21.97, 21.89) * mm});
            skArc(sketch, "E171", {"start": v(-25.3, 18.38) * mm, "mid": v(-25.77, 17.64) * mm, "end": v(-25.88, 16.76) * mm});
            skArc(sketch, "E172", {"start": v(-21.76, 21.92) * mm, "mid": v(-21.77, 21.91) * mm, "end": v(-21.78, 21.9) * mm});
            skArc(sketch, "E173", {"start": v(-21.78, -21.9) * mm, "mid": v(-21.77, -21.91) * mm, "end": v(-21.76, -21.92) * mm});
            skLineSegment(sketch, "E174", {"start": v(-25.38, -18.3) * mm, "end": v(-21.8, -21.89) * mm});
            skLineSegment(sketch, "E175", {"start": v(-23.66, -14) * mm, "end": v(-23.66, -15) * mm});
            skLineSegment(sketch, "E176", {"start": v(-21.66, -14) * mm, "end": v(-21.66, -15) * mm});
            skLineSegment(sketch, "E177", {"start": v(-23.66, 15.1) * mm, "end": v(-23.66, 14.1) * mm});
            skLineSegment(sketch, "E178", {"start": v(-21.66, 15.1) * mm, "end": v(-21.66, 14.1) * mm});
            skLineSegment(sketch, "E179", {"start": v(-25.97, -16.73) * mm, "end": v(-25.97, -16.8) * mm});
            skArc(sketch, "E180", {"start": v(-25.97, -16.8) * mm, "mid": v(-25.83, -17.6) * mm, "end": v(-25.38, -18.3) * mm});
            skCircle(sketch, "E181", {"center": v(15.34, 15.25) * mm, "radius": 1.5 * mm});
            skCircle(sketch, "E182", {"center": v(15.34, -15.25) * mm, "radius": 1.5 * mm});
            skCircle(sketch, "E183", {"center": v(-15.16, -15.25) * mm, "radius": 1.5 * mm});
            skCircle(sketch, "E184", {"center": v(-15.16, 15.25) * mm, "radius": 1.5 * mm});
            skCircle(sketch, "E185", {"center": v(19.86, -19.77) * mm, "radius": 1.5 * mm});
            skCircle(sketch, "E186", {"center": v(19.86, 19.77) * mm, "radius": 1.5 * mm});
            skCircle(sketch, "E187", {"center": v(-19.67, 19.77) * mm, "radius": 1.5 * mm});
            skCircle(sketch, "E188", {"center": v(-19.63, -19.8) * mm, "radius": 1.5 * mm});
            skSolve(sketch);
        }
        {
            var Q0;
            Q0 = qSketchRegion(id + "F12", true);
            extrude(context, id + "F13", {"entities" : qUnion([Q0]), "depth" : 1.5 * mm});
        }
        {
            var Q0;
            Q0=makeQuery(id+"F13.opExtrude","SWEPT_BODY",BODY,{"disambiguationData":[OSD([sQuery(id+"F12.wireOp",EDGE,"E118"),sQuery(id+"F12.wireOp",EDGE,"E119"),sQuery(id+"F12.wireOp",EDGE,"E120"),sQuery(id+"F12.wireOp",EDGE,"E121"),sQuery(id+"F12.wireOp",EDGE,"E122"),sQuery(id+"F12.wireOp",EDGE,"E123"),sQuery(id+"F12.wireOp",EDGE,"E124"),sQuery(id+"F12.wireOp",EDGE,"E125"),sQuery(id+"F12.wireOp",EDGE,"E126"),sQuery(id+"F12.wireOp",EDGE,"E127"),sQuery(id+"F12.wireOp",EDGE,"E128"),sQuery(id+"F12.wireOp",EDGE,"E129"),sQuery(id+"F12.wireOp",EDGE,"E130"),sQuery(id+"F12.wireOp",EDGE,"E131"),sQuery(id+"F12.wireOp",EDGE,"E132"),sQuery(id+"F12.wireOp",EDGE,"E133"),sQuery(id+"F12.wireOp",EDGE,"E134"),sQuery(id+"F12.wireOp",EDGE,"E135"),sQuery(id+"F12.wireOp",EDGE,"E136"),sQuery(id+"F12.wireOp",EDGE,"E137"),sQuery(id+"F12.wireOp",EDGE,"E138"),sQuery(id+"F12.wireOp",EDGE,"E139"),sQuery(id+"F12.wireOp",EDGE,"E140"),sQuery(id+"F12.wireOp",EDGE,"E141"),sQuery(id+"F12.wireOp",EDGE,"E142"),sQuery(id+"F12.wireOp",EDGE,"E143"),sQuery(id+"F12.wireOp",EDGE,"E144"),sQuery(id+"F12.wireOp",EDGE,"E145"),sQuery(id+"F12.wireOp",EDGE,"E146"),sQuery(id+"F12.wireOp",EDGE,"E147"),sQuery(id+"F12.wireOp",EDGE,"E148"),sQuery(id+"F12.wireOp",EDGE,"E149"),sQuery(id+"F12.wireOp",EDGE,"E150"),sQuery(id+"F12.wireOp",EDGE,"E151"),sQuery(id+"F12.wireOp",EDGE,"E152"),sQuery(id+"F12.wireOp",EDGE,"E153"),sQuery(id+"F12.wireOp",EDGE,"E154"),sQuery(id+"F12.wireOp",EDGE,"E155"),sQuery(id+"F12.wireOp",EDGE,"E156"),sQuery(id+"F12.wireOp",EDGE,"E157"),sQuery(id+"F12.wireOp",EDGE,"E158"),sQuery(id+"F12.wireOp",EDGE,"E159"),sQuery(id+"F12.wireOp",EDGE,"E160"),sQuery(id+"F12.wireOp",EDGE,"E161"),sQuery(id+"F12.wireOp",EDGE,"E162"),sQuery(id+"F12.wireOp",EDGE,"E163"),sQuery(id+"F12.wireOp",EDGE,"E164"),sQuery(id+"F12.wireOp",EDGE,"E165"),sQuery(id+"F12.wireOp",EDGE,"E166"),sQuery(id+"F12.wireOp",EDGE,"E167"),sQuery(id+"F12.wireOp",EDGE,"E168"),sQuery(id+"F12.wireOp",EDGE,"E169"),sQuery(id+"F12.wireOp",EDGE,"E170"),sQuery(id+"F12.wireOp",EDGE,"E171"),sQuery(id+"F12.wireOp",EDGE,"E172"),sQuery(id+"F12.wireOp",EDGE,"E173"),sQuery(id+"F12.wireOp",EDGE,"E174"),sQuery(id+"F12.wireOp",EDGE,"E175"),sQuery(id+"F12.wireOp",EDGE,"E176"),sQuery(id+"F12.wireOp",EDGE,"E177"),sQuery(id+"F12.wireOp",EDGE,"E178"),sQuery(id+"F12.wireOp",EDGE,"E179"),sQuery(id+"F12.wireOp",EDGE,"E180"),sQuery(id+"F12.wireOp",EDGE,"E181"),sQuery(id+"F12.wireOp",EDGE,"E182"),sQuery(id+"F12.wireOp",EDGE,"E183"),sQuery(id+"F12.wireOp",EDGE,"E184"),sQuery(id+"F12.wireOp",EDGE,"E185"),sQuery(id+"F12.wireOp",EDGE,"E186"),sQuery(id+"F12.wireOp",EDGE,"E187"),sQuery(id+"F12.wireOp",EDGE,"E188")])]});
            transform(context, id + "F14", {"entities" : qUnion([Q0]), "transformType" : TransformType.TRANSLATION_3D, "dx" : 0 * mm, "dy" : 0 * mm, "dz" : 4 * mm, "makeCopy" : false});
        }
        {
            var Q0;
            Q0=qCreatedBy(makeId("Top.planeOp"),FACE);
            var sketch = newSketch(context, id + "F15", { "sketchPlane" : qUnion([Q0])});
            skLineSegment(sketch, "E189", {"start": v(-14.16, -15) * mm, "end": v(-16.16, -15) * mm});
            skLineSegment(sketch, "E190", {"start": v(-14.16, 15.1) * mm, "end": v(-16.16, 15.1) * mm});
            skLineSegment(sketch, "E191", {"start": v(-14.16, 14.1) * mm, "end": v(-16.16, 14.1) * mm});
            skLineSegment(sketch, "E192", {"start": v(-21.66, -14) * mm, "end": v(-23.66, -14) * mm});
            skLineSegment(sketch, "E193", {"start": v(-21.66, -15) * mm, "end": v(-23.66, -15) * mm});
            skLineSegment(sketch, "E194", {"start": v(-21.66, 15.1) * mm, "end": v(-23.66, 15.1) * mm});
            skLineSegment(sketch, "E195", {"start": v(-21.66, 14.1) * mm, "end": v(-23.66, 14.1) * mm});
            skLineSegment(sketch, "E196", {"start": v(-21.78, -21.9) * mm, "end": v(-25.39, -18.3) * mm});
            skLineSegment(sketch, "E197", {"start": v(-21.78, 21.9) * mm, "end": v(-25.3, 18.38) * mm});
            skLineSegment(sketch, "E198", {"start": v(-14.16, -14) * mm, "end": v(-16.16, -14) * mm});
            skLineSegment(sketch, "E199", {"start": v(-25.88, 16.76) * mm, "end": v(-24.97, 12.73) * mm});
            skLineSegment(sketch, "E200", {"start": v(-24.97, 12.73) * mm, "end": v(-23.5, 8.88) * mm});
            skLineSegment(sketch, "E201", {"start": v(-23.5, 8.88) * mm, "end": v(-22, 5.17) * mm});
            skLineSegment(sketch, "E202", {"start": v(-22, 5.17) * mm, "end": v(-21.02, 1.6) * mm});
            skLineSegment(sketch, "E203", {"start": v(-21.02, 1.6) * mm, "end": v(-21.1, -1.9) * mm});
            skLineSegment(sketch, "E204", {"start": v(-21.1, -1.9) * mm, "end": v(-22.18, -5.3) * mm});
            skLineSegment(sketch, "E205", {"start": v(-22.18, -5.3) * mm, "end": v(-23.7, -8.82) * mm});
            skLineSegment(sketch, "E206", {"start": v(-23.7, -8.82) * mm, "end": v(-25.15, -12.6) * mm});
            skLineSegment(sketch, "E207", {"start": v(-25.15, -12.6) * mm, "end": v(-25.97, -16.73) * mm});
            skLineSegment(sketch, "E208", {"start": v(21.98, -21.89) * mm, "end": v(20.2, -22.93) * mm});
            skLineSegment(sketch, "E209", {"start": v(20.2, -22.93) * mm, "end": v(18.03, -23.06) * mm});
            skLineSegment(sketch, "E210", {"start": v(18.03, -23.06) * mm, "end": v(15.54, -22.51) * mm});
            skLineSegment(sketch, "E211", {"start": v(15.54, -22.51) * mm, "end": v(12.78, -21.53) * mm});
            skLineSegment(sketch, "E212", {"start": v(12.78, -21.53) * mm, "end": v(8.77, -19.95) * mm});
            skLineSegment(sketch, "E213", {"start": v(8.77, -19.95) * mm, "end": v(4.5, -18.58) * mm});
            skLineSegment(sketch, "E214", {"start": v(4.5, -18.58) * mm, "end": v(0.1, -18) * mm});
            skLineSegment(sketch, "E215", {"start": v(0.1, -18) * mm, "end": v(-4.31, -18.57) * mm});
            skLineSegment(sketch, "E216", {"start": v(-4.31, -18.57) * mm, "end": v(-8.59, -19.93) * mm});
            skLineSegment(sketch, "E217", {"start": v(-8.59, -19.93) * mm, "end": v(-12.6, -21.5) * mm});
            skLineSegment(sketch, "E218", {"start": v(-12.6, -21.5) * mm, "end": v(-15.37, -22.48) * mm});
            skLineSegment(sketch, "E219", {"start": v(-15.37, -22.48) * mm, "end": v(-17.86, -23.04) * mm});
            skLineSegment(sketch, "E220", {"start": v(-17.86, -23.04) * mm, "end": v(-20, -22.92) * mm});
            skLineSegment(sketch, "E221", {"start": v(-20, -22.92) * mm, "end": v(-21.76, -21.92) * mm});
            skLineSegment(sketch, "E222", {"start": v(-21.76, 21.92) * mm, "end": v(-19.99, 22.94) * mm});
            skLineSegment(sketch, "E223", {"start": v(-19.99, 22.94) * mm, "end": v(-17.84, 23.06) * mm});
            skLineSegment(sketch, "E224", {"start": v(-17.84, 23.06) * mm, "end": v(-15.35, 22.51) * mm});
            skLineSegment(sketch, "E225", {"start": v(-15.35, 22.51) * mm, "end": v(-12.6, 21.53) * mm});
            skLineSegment(sketch, "E226", {"start": v(-12.6, 21.53) * mm, "end": v(-8.58, 19.95) * mm});
            skLineSegment(sketch, "E227", {"start": v(-8.58, 19.95) * mm, "end": v(-4.31, 18.58) * mm});
            skLineSegment(sketch, "E228", {"start": v(-4.31, 18.58) * mm, "end": v(0.1, 18) * mm});
            skLineSegment(sketch, "E229", {"start": v(0.1, 18) * mm, "end": v(4.5, 18.57) * mm});
            skLineSegment(sketch, "E230", {"start": v(4.5, 18.57) * mm, "end": v(8.78, 19.92) * mm});
            skLineSegment(sketch, "E231", {"start": v(8.78, 19.92) * mm, "end": v(12.8, 21.5) * mm});
            skLineSegment(sketch, "E232", {"start": v(12.8, 21.5) * mm, "end": v(15.57, 22.47) * mm});
            skLineSegment(sketch, "E233", {"start": v(15.57, 22.47) * mm, "end": v(18.06, 23.03) * mm});
            skLineSegment(sketch, "E234", {"start": v(18.06, 23.03) * mm, "end": v(20.2, 22.9) * mm});
            skLineSegment(sketch, "E235", {"start": v(20.2, 22.9) * mm, "end": v(22.24, 21.67) * mm});
            skLineSegment(sketch, "E236", {"start": v(22.24, 21.67) * mm, "end": v(24.06, 18.68) * mm});
            skLineSegment(sketch, "E237", {"start": v(24.06, 18.68) * mm, "end": v(25.26, 14.51) * mm});
            skLineSegment(sketch, "E238", {"start": v(25.26, 14.51) * mm, "end": v(25.8, 9.64) * mm});
            skLineSegment(sketch, "E239", {"start": v(25.8, 9.64) * mm, "end": v(25.97, 3.34) * mm});
            skLineSegment(sketch, "E240", {"start": v(25.97, 3.34) * mm, "end": v(25.97, -3.19) * mm});
            skLineSegment(sketch, "E241", {"start": v(25.97, -3.19) * mm, "end": v(25.82, -9.52) * mm});
            skLineSegment(sketch, "E242", {"start": v(25.82, -9.52) * mm, "end": v(25.12, -15.22) * mm});
            skLineSegment(sketch, "E243", {"start": v(25.12, -15.22) * mm, "end": v(23.94, -18.98) * mm});
            skLineSegment(sketch, "E244", {"start": v(23.94, -18.98) * mm, "end": v(21.98, -21.89) * mm});
            skCircle(sketch, "E245", {"center": v(21.78, 0) * mm, "radius": 2.5 * mm});
            skArc(sketch, "E246", {"start": v(-25.3, 18.38) * mm, "mid": v(-25.77, 17.64) * mm, "end": v(-25.88, 16.76) * mm});
            skArc(sketch, "E247", {"start": v(-21.76, 21.92) * mm, "mid": v(-21.77, 21.91) * mm, "end": v(-21.78, 21.9) * mm});
            skArc(sketch, "E248", {"start": v(-21.78, -21.9) * mm, "mid": v(-21.77, -21.91) * mm, "end": v(-21.76, -21.92) * mm});
            skLineSegment(sketch, "E249", {"start": v(-25.38, -18.3) * mm, "end": v(-21.8, -21.89) * mm});
            skLineSegment(sketch, "E250", {"start": v(-23.66, -14) * mm, "end": v(-23.66, -15) * mm});
            skLineSegment(sketch, "E251", {"start": v(-21.66, -14) * mm, "end": v(-21.66, -15) * mm});
            skLineSegment(sketch, "E252", {"start": v(-23.66, 15.1) * mm, "end": v(-23.66, 14.1) * mm});
            skLineSegment(sketch, "E253", {"start": v(-21.66, 15.1) * mm, "end": v(-21.66, 14.1) * mm});
            skLineSegment(sketch, "E254", {"start": v(-16.16, -14) * mm, "end": v(-16.16, -15) * mm});
            skLineSegment(sketch, "E255", {"start": v(-14.16, -14) * mm, "end": v(-14.16, -15) * mm});
            skLineSegment(sketch, "E256", {"start": v(-14.16, 15.1) * mm, "end": v(-14.16, 14.1) * mm});
            skLineSegment(sketch, "E257", {"start": v(-16.16, 15.1) * mm, "end": v(-16.16, 14.1) * mm});
            skLineSegment(sketch, "E258", {"start": v(-25.97, -16.73) * mm, "end": v(-25.97, -16.8) * mm});
            skArc(sketch, "E259", {"start": v(-25.97, -16.8) * mm, "mid": v(-25.83, -17.6) * mm, "end": v(-25.38, -18.3) * mm});
            skCircle(sketch, "E260", {"center": v(19.86, -19.77) * mm, "radius": 1.5 * mm});
            skCircle(sketch, "E261", {"center": v(19.86, 19.77) * mm, "radius": 1.5 * mm});
            skCircle(sketch, "E262", {"center": v(-19.67, 19.77) * mm, "radius": 1.5 * mm});
            skCircle(sketch, "E263", {"center": v(-19.63, -19.8) * mm, "radius": 1.5 * mm});
            skSolve(sketch);
        }
        {
            var Q0;
            Q0 = qSketchRegion(id + "F15", true);
            extrude(context, id + "F16", {"entities" : qUnion([Q0]), "depth" : 1.5 * mm});
        }
        {
            var Q0;
            Q0=makeQuery(id+"F16.opExtrude","SWEPT_BODY",BODY,{"disambiguationData":[OSD([sQuery(id+"F15.wireOp",EDGE,"E189"),sQuery(id+"F15.wireOp",EDGE,"E190"),sQuery(id+"F15.wireOp",EDGE,"E191"),sQuery(id+"F15.wireOp",EDGE,"E192"),sQuery(id+"F15.wireOp",EDGE,"E193"),sQuery(id+"F15.wireOp",EDGE,"E194"),sQuery(id+"F15.wireOp",EDGE,"E195"),sQuery(id+"F15.wireOp",EDGE,"E196"),sQuery(id+"F15.wireOp",EDGE,"E197"),sQuery(id+"F15.wireOp",EDGE,"E198"),sQuery(id+"F15.wireOp",EDGE,"E199"),sQuery(id+"F15.wireOp",EDGE,"E200"),sQuery(id+"F15.wireOp",EDGE,"E201"),sQuery(id+"F15.wireOp",EDGE,"E202"),sQuery(id+"F15.wireOp",EDGE,"E203"),sQuery(id+"F15.wireOp",EDGE,"E204"),sQuery(id+"F15.wireOp",EDGE,"E205"),sQuery(id+"F15.wireOp",EDGE,"E206"),sQuery(id+"F15.wireOp",EDGE,"E207"),sQuery(id+"F15.wireOp",EDGE,"E208"),sQuery(id+"F15.wireOp",EDGE,"E209"),sQuery(id+"F15.wireOp",EDGE,"E210"),sQuery(id+"F15.wireOp",EDGE,"E211"),sQuery(id+"F15.wireOp",EDGE,"E212"),sQuery(id+"F15.wireOp",EDGE,"E213"),sQuery(id+"F15.wireOp",EDGE,"E214"),sQuery(id+"F15.wireOp",EDGE,"E215"),sQuery(id+"F15.wireOp",EDGE,"E216"),sQuery(id+"F15.wireOp",EDGE,"E217"),sQuery(id+"F15.wireOp",EDGE,"E218"),sQuery(id+"F15.wireOp",EDGE,"E219"),sQuery(id+"F15.wireOp",EDGE,"E220"),sQuery(id+"F15.wireOp",EDGE,"E221"),sQuery(id+"F15.wireOp",EDGE,"E222"),sQuery(id+"F15.wireOp",EDGE,"E223"),sQuery(id+"F15.wireOp",EDGE,"E224"),sQuery(id+"F15.wireOp",EDGE,"E225"),sQuery(id+"F15.wireOp",EDGE,"E226"),sQuery(id+"F15.wireOp",EDGE,"E227"),sQuery(id+"F15.wireOp",EDGE,"E228"),sQuery(id+"F15.wireOp",EDGE,"E229"),sQuery(id+"F15.wireOp",EDGE,"E230"),sQuery(id+"F15.wireOp",EDGE,"E231"),sQuery(id+"F15.wireOp",EDGE,"E232"),sQuery(id+"F15.wireOp",EDGE,"E233"),sQuery(id+"F15.wireOp",EDGE,"E234"),sQuery(id+"F15.wireOp",EDGE,"E235"),sQuery(id+"F15.wireOp",EDGE,"E236"),sQuery(id+"F15.wireOp",EDGE,"E237"),sQuery(id+"F15.wireOp",EDGE,"E238"),sQuery(id+"F15.wireOp",EDGE,"E239"),sQuery(id+"F15.wireOp",EDGE,"E240"),sQuery(id+"F15.wireOp",EDGE,"E241"),sQuery(id+"F15.wireOp",EDGE,"E242"),sQuery(id+"F15.wireOp",EDGE,"E243"),sQuery(id+"F15.wireOp",EDGE,"E244"),sQuery(id+"F15.wireOp",EDGE,"E245"),sQuery(id+"F15.wireOp",EDGE,"E246"),sQuery(id+"F15.wireOp",EDGE,"E247"),sQuery(id+"F15.wireOp",EDGE,"E248"),sQuery(id+"F15.wireOp",EDGE,"E249"),sQuery(id+"F15.wireOp",EDGE,"E250"),sQuery(id+"F15.wireOp",EDGE,"E251"),sQuery(id+"F15.wireOp",EDGE,"E252"),sQuery(id+"F15.wireOp",EDGE,"E253"),sQuery(id+"F15.wireOp",EDGE,"E254"),sQuery(id+"F15.wireOp",EDGE,"E255"),sQuery(id+"F15.wireOp",EDGE,"E256"),sQuery(id+"F15.wireOp",EDGE,"E257"),sQuery(id+"F15.wireOp",EDGE,"E258"),sQuery(id+"F15.wireOp",EDGE,"E259"),sQuery(id+"F15.wireOp",EDGE,"E260"),sQuery(id+"F15.wireOp",EDGE,"E261"),sQuery(id+"F15.wireOp",EDGE,"E262"),sQuery(id+"F15.wireOp",EDGE,"E263")])]});
            transform(context, id + "F17", {"entities" : qUnion([Q0]), "transformType" : TransformType.TRANSLATION_3D, "dx" : 0 * mm, "dy" : 0 * mm, "dz" : 40.5 * mm, "makeCopy" : false});
        }
        {
            var Q0;
            Q0=qCreatedBy(makeId("Front.planeOp"),FACE);
            var sketch = newSketch(context, id + "F18", { "sketchPlane" : qUnion([Q0])});
            skLineSegment(sketch, "E264", {"start": v(-5.75, 17.5) * mm, "end": v(-5.75, -17.5) * mm});
            skLineSegment(sketch, "E265", {"start": v(-5.75, -17.5) * mm, "end": v(-4.75, -17.5) * mm});
            skLineSegment(sketch, "E266", {"start": v(-4.75, -17.5) * mm, "end": v(-4.75, -18.5) * mm});
            skLineSegment(sketch, "E267", {"start": v(-4.75, -18.5) * mm, "end": v(-2.75, -18.5) * mm});
            skLineSegment(sketch, "E268", {"start": v(-2.75, -18.5) * mm, "end": v(-2.75, -17.5) * mm});
            skLineSegment(sketch, "E269", {"start": v(-2.75, -17.5) * mm, "end": v(-1.75, -17.5) * mm});
            skLineSegment(sketch, "E270", {"start": v(-5.75, 17.5) * mm, "end": v(-4.75, 17.5) * mm});
            skLineSegment(sketch, "E271", {"start": v(-2.75, 18.5) * mm, "end": v(-2.75, 17.5) * mm});
            skLineSegment(sketch, "E272", {"start": v(-4.75, 17.5) * mm, "end": v(-4.75, 18.5) * mm});
            skLineSegment(sketch, "E273", {"start": v(-4.75, 18.5) * mm, "end": v(-2.75, 18.5) * mm});
            skLineSegment(sketch, "E274", {"start": v(-2.75, 17.5) * mm, "end": v(2.75, 17.5) * mm});
            skLineSegment(sketch, "E275", {"start": v(2.75, 17.5) * mm, "end": v(2.75, 18.5) * mm});
            skLineSegment(sketch, "E276", {"start": v(2.75, 18.5) * mm, "end": v(4.75, 18.5) * mm});
            skLineSegment(sketch, "E277", {"start": v(4.75, 18.5) * mm, "end": v(4.75, 17.5) * mm});
            skLineSegment(sketch, "E278", {"start": v(4.75, 17.5) * mm, "end": v(5.75, 17.5) * mm});
            skLineSegment(sketch, "E279", {"start": v(-1.75, -17.5) * mm, "end": v(5.75, 17.5) * mm});
            skCircle(sketch, "E280", {"center": v(-2.75, 0) * mm, "radius": 1.5 * mm});
            skSolve(sketch);
        }
        {
            var Q0;
            Q0=makeQuery(id+"F18.imprint","IMPRINT",FACE,{"disambiguationData":[TD([[makeQuery(id+"F18.imprint","IMPRINT",EDGE,{"derivedFrom":sQuery(id+"F18.wireOp",EDGE,"E264")}),1.0]])]});
            extrude(context, id + "F19", {"entities" : qUnion([Q0]), "depth" : 1 * mm});
        }
        {
            var Q0;
            Q0=makeQuery(id+"F19.opExtrude","SWEPT_BODY",BODY,{"disambiguationData":[OSD([sQuery(id+"F18.wireOp",EDGE,"E264"),sQuery(id+"F18.wireOp",EDGE,"E265"),sQuery(id+"F18.wireOp",EDGE,"E266"),sQuery(id+"F18.wireOp",EDGE,"E267"),sQuery(id+"F18.wireOp",EDGE,"E268"),sQuery(id+"F18.wireOp",EDGE,"E269"),sQuery(id+"F18.wireOp",EDGE,"E270"),sQuery(id+"F18.wireOp",EDGE,"E271"),sQuery(id+"F18.wireOp",EDGE,"E272"),sQuery(id+"F18.wireOp",EDGE,"E273"),sQuery(id+"F18.wireOp",EDGE,"E274"),sQuery(id+"F18.wireOp",EDGE,"E275"),sQuery(id+"F18.wireOp",EDGE,"E276"),sQuery(id+"F18.wireOp",EDGE,"E277"),sQuery(id+"F18.wireOp",EDGE,"E278"),sQuery(id+"F18.wireOp",EDGE,"E279"),sQuery(id+"F18.wireOp",EDGE,"E280")])]});
            transform(context, id + "F20", {"entities" : qUnion([Q0]), "transformType" : TransformType.TRANSLATION_3D, "dx" : -19.03 * mm, "dy" : -14.04 * mm, "dz" : 23 * mm, "makeCopy" : false});
        }
        {
            var Q0;
            Q0 = qSketchRegion(id + "F18", true);
            extrude(context, id + "F21", {"entities" : qUnion([Q0]), "depth" : 1 * mm});
        }
        {
            var Q0;
            Q0=makeQuery(id+"F21.opExtrude","SWEPT_BODY",BODY,{"disambiguationData":[OSD([sQuery(id+"F18.wireOp",EDGE,"E264"),sQuery(id+"F18.wireOp",EDGE,"E265"),sQuery(id+"F18.wireOp",EDGE,"E266"),sQuery(id+"F18.wireOp",EDGE,"E267"),sQuery(id+"F18.wireOp",EDGE,"E268"),sQuery(id+"F18.wireOp",EDGE,"E269"),sQuery(id+"F18.wireOp",EDGE,"E270"),sQuery(id+"F18.wireOp",EDGE,"E271"),sQuery(id+"F18.wireOp",EDGE,"E272"),sQuery(id+"F18.wireOp",EDGE,"E273"),sQuery(id+"F18.wireOp",EDGE,"E274"),sQuery(id+"F18.wireOp",EDGE,"E275"),sQuery(id+"F18.wireOp",EDGE,"E276"),sQuery(id+"F18.wireOp",EDGE,"E277"),sQuery(id+"F18.wireOp",EDGE,"E278"),sQuery(id+"F18.wireOp",EDGE,"E279"),sQuery(id+"F18.wireOp",EDGE,"E280")])]});
            transform(context, id + "F22", {"entities" : qUnion([Q0]), "transformType" : TransformType.TRANSLATION_3D, "dx" : -18.9 * mm, "dy" : 15.1 * mm, "dz" : 23.03 * mm, "makeCopy" : false});
        }
        {
            var Q0;
            Q0=qCreatedBy(makeId("Top.planeOp"),FACE);
            var sketch = newSketch(context, id + "F23", { "sketchPlane" : qUnion([Q0])});
            skCircle(sketch, "E281", {"center": v(-19.7, -19.82) * mm, "radius": 1.51 * mm});
            skCircle(sketch, "E282", {"center": v(19.78, -19.78) * mm, "radius": 1.52 * mm});
            skCircle(sketch, "E283", {"center": v(19.87, 19.75) * mm, "radius": 1.52 * mm});
            skCircle(sketch, "E284", {"center": v(-19.75, 19.75) * mm, "radius": 1.5 * mm});
            skSolve(sketch);
        }
        {
            var Q0;
            Q0 = qSketchRegion(id + "F23", true);
            extrude(context, id + "F24", {"entities" : qUnion([Q0]), "depth" : 41.8 * mm});
        }
    });
